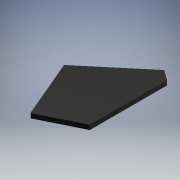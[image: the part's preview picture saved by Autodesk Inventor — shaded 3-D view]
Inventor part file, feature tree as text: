
AUTODESK INVENTOR PART (.ipt)
format: ipt  version: 2018 (Build 220112000, 112)  size: 99,840 bytes
history: native  units: mm
features: extrude x1, sketch x1
ambient origin geometry x8: Origin, YZ Plane, XZ Plane, XY Plane, X Axis, Y Axis, Z Axis, Center Point
bodies: Solid1 (feature_tree)
feature tree (2):
  extrude  "Extrusion1"  Depth=3.0mm TaperAngle=0.0deg
  sketch  "Sketch1"  dims[d0=21.816616mm d1=20.257173mm d2=8.726646mm d3=4.014257mm d4=18.58376mm d5=45.750155mm d6=13.725103mm d7=28.308135mm d8=13.269457mm d9=3.0mm d10=0.0mm]
